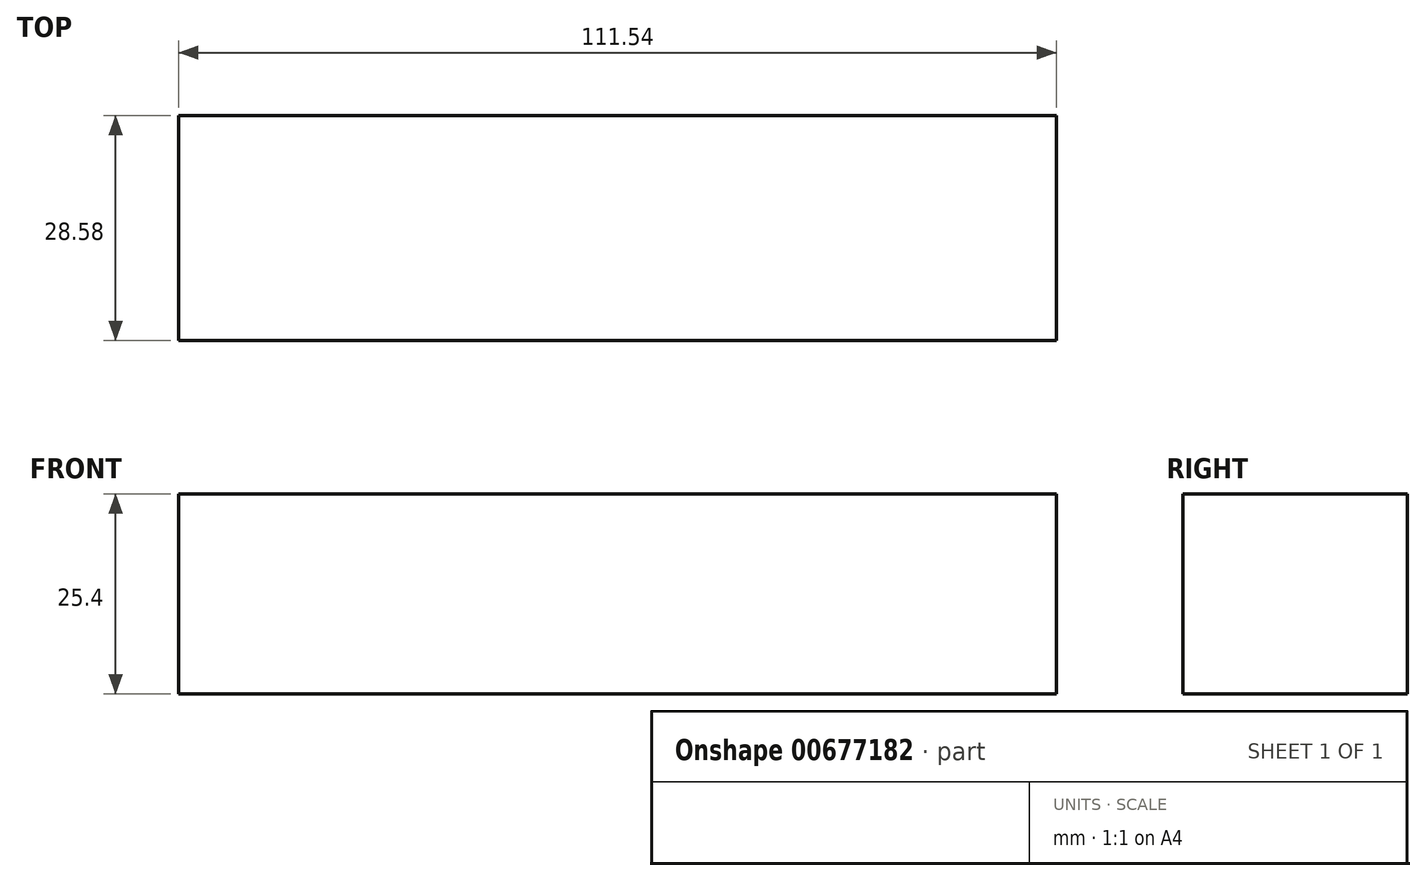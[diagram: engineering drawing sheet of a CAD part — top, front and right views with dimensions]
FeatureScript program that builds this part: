
annotation { "Feature Type Name" : "Feature", "Feature Type Description" : "" }
export const myFeature = defineFeature(function(context is Context, id is Id, definition is map)
    precondition{}
    {
        {
            var Q0;
            Q0=qCreatedBy(makeId("Top.planeOp"),FACE);
            var sketch = newSketch(context, id + "F0", { "sketchPlane" : qUnion([Q0])});
            skLineSegment(sketch, "E0.bottom", {"start": v(55.77, 14.29) * mm, "end": v(-55.77, 14.29) * mm});
            skLineSegment(sketch, "E0.top", {"start": v(55.77, -14.29) * mm, "end": v(-55.77, -14.29) * mm});
            skLineSegment(sketch, "E0.left", {"start": v(55.77, 14.29) * mm, "end": v(55.77, -14.29) * mm});
            skLineSegment(sketch, "E0.right", {"start": v(-55.77, 14.29) * mm, "end": v(-55.77, -14.29) * mm});
            skPoint(sketch, "E0.middle", {"position": v(0, 0) * mm});
            skSolve(sketch);
        }
        {
            var Q0;
            Q0 = qSketchRegion(id + "F0", true);
            extrude(context, id + "F1", {"entities" : qUnion([Q0]), "depth" : 25.4 * mm, "offsetDistance" : 25.4 * mm});
        }
    });
